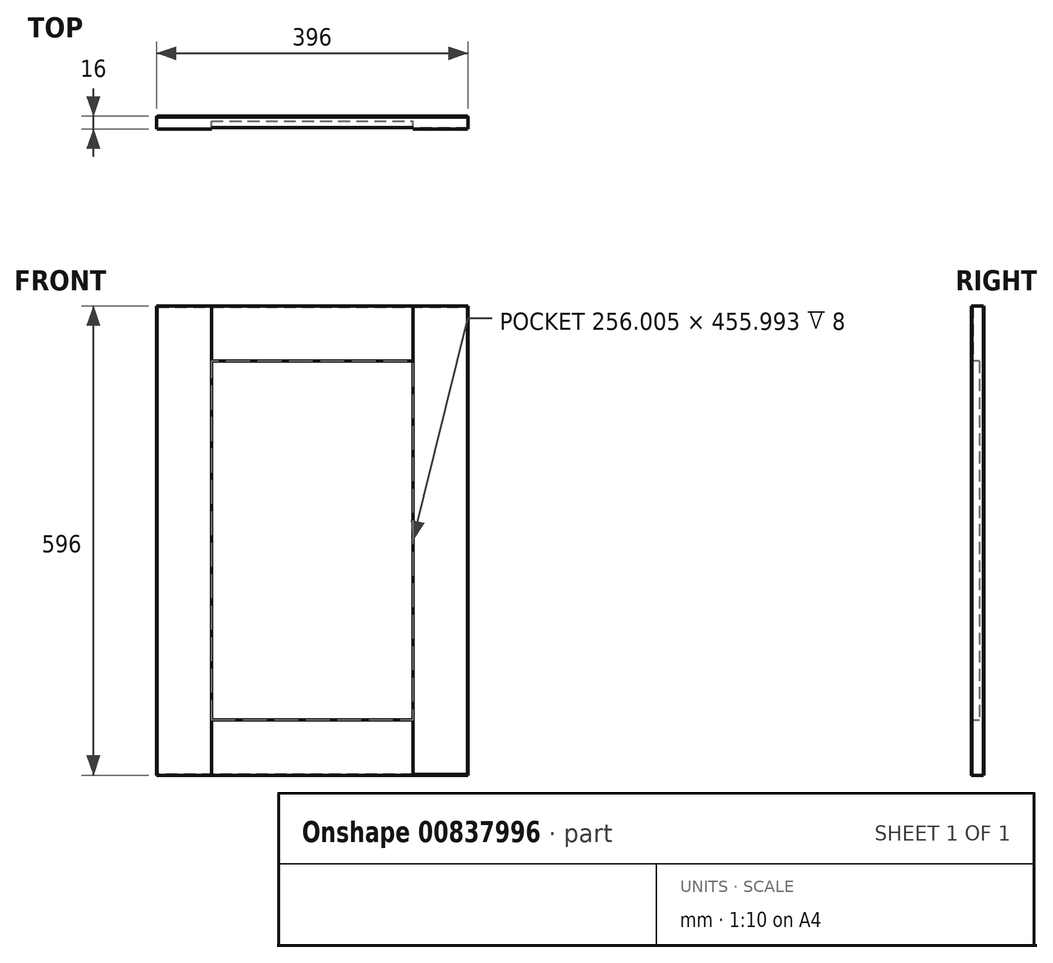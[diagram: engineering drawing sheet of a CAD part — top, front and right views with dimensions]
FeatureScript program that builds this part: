
annotation { "Feature Type Name" : "Feature", "Feature Type Description" : "" }
export const myFeature = defineFeature(function(context is Context, id is Id, definition is map)
    precondition{}
    {
        {
            var Q0;
            Q0=qCreatedBy(makeId("Front.planeOp"),FACE);
            var sketch = newSketch(context, id + "F0", { "sketchPlane" : qUnion([Q0])});
            skLineSegment(sketch, "E0.bottom", {"start": v(0, 0) * mm, "end": v(35.9, 0) * mm});
            skLineSegment(sketch, "E0.top", {"start": v(0, 30.12) * mm, "end": v(35.9, 30.12) * mm});
            skLineSegment(sketch, "E0.left", {"start": v(0, 0) * mm, "end": v(0, 30.12) * mm});
            skLineSegment(sketch, "E0.right", {"start": v(35.9, 0) * mm, "end": v(35.9, 30.12) * mm});
            skSolve(sketch);
        }
        {
            var Q0;
            Q0=makeQuery(id+"F0.imprint","IMPRINT",FACE,{"disambiguationData":[TD([[makeQuery(id+"F0.imprint","IMPRINT",EDGE,{"derivedFrom":sQuery(id+"F0.wireOp",EDGE,"E0.bottom")}),1.0]])]});
            extrude(context, id + "F1", {"entities" : qUnion([Q0]), "depth" : 16 * mm, "offsetDistance" : 25.4 * mm});
        }
        {
            var Q0;
            Q0=makeQuery(id+"F1.opExtrude","SWEPT_FACE",FACE,{"disambiguationData":[OSD([sQuery(id+"F0.wireOp",EDGE,"E0.left")])]});
            extrude(context, id + "F2", {"entities" : qUnion([Q0]), "operationType" : NewBodyOperationType.ADD, "oppositeDirection" : true, "depth" : 196 * mm, "offsetDistance" : 25 * mm});
        }
        {
            var Q0;
            {var subQ0=sQuery(id+"F0.wireOp",EDGE,"E0.bottom");Q0=makeQuery(id+"F2.boolean.opBoolean","MERGE",FACE,{"derivedFrom":[makeQuery(id+"F1.opExtrude","SWEPT_FACE",FACE,{"disambiguationData":[OSD([subQ0])]}),makeQuery(id+"F2.opExtrude","SWEPT_FACE",FACE,{"disambiguationData":[OSD([subQ0,sQuery(id+"F0.wireOp",EDGE,"E0.left")])]})]});}
            extrude(context, id + "F3", {"entities" : qUnion([Q0]), "operationType" : NewBodyOperationType.ADD, "oppositeDirection" : true, "depth" : 796 * mm, "offsetDistance" : 25 * mm});
        }
        {
            var Q0;
            {var subQ0=sQuery(id+"F0.wireOp",EDGE,"E0.left");var subQ1=sQuery(id+"F0.wireOp",EDGE,"E0.bottom");Q0=makeQuery(id+"F3.boolean.opBoolean","MERGE",FACE,{"derivedFrom":[makeQuery(id+"F2.boolean.opBoolean","MERGE",FACE,{"derivedFrom":[makeQuery(id+"F1.opExtrude","CAP_FACE",FACE,{"disambiguationData":[OSD([subQ1,sQuery(id+"F0.wireOp",EDGE,"E0.top"),subQ0,sQuery(id+"F0.wireOp",EDGE,"E0.right")])],"isStart":false}),makeQuery(id+"F2.opExtrude","SWEPT_FACE",FACE,{"disambiguationData":[OSD([subQ0]),TDD([makeQuery(id+"F1.opExtrude","CAP_EDGE",EDGE,{"disambiguationData":[OSD([subQ0])],"isStart":false})])]})]}),makeQuery(id+"F3.opExtrude","SWEPT_FACE",FACE,{"disambiguationData":[OSD([subQ1,subQ0]),TDD([makeQuery(id+"F2.boolean.opBoolean","MERGE",EDGE,{"derivedFrom":[makeQuery(id+"F1.opExtrude","CAP_EDGE",EDGE,{"disambiguationData":[OSD([subQ1])],"isStart":false}),makeQuery(id+"F2.opExtrude","SWEPT_EDGE",EDGE,{"disambiguationData":[OSD([subQ1,subQ0]),TDD([makeQuery(id+"F1.opExtrude","CAP_VERTEX",VERTEX,{"disambiguationData":[OSD([subQ1,subQ0])],"isStart":false})])]})]})])]})]});}
            var sketch = newSketch(context, id + "F4", { "sketchPlane" : qUnion([Q0])});
            skLineSegment(sketch, "E1.bottom", {"start": v(0, 796) * mm, "end": v(42.19, 796) * mm});
            skLineSegment(sketch, "E1.top", {"start": v(0, 751.57) * mm, "end": v(42.19, 751.57) * mm});
            skLineSegment(sketch, "E1.left", {"start": v(0, 796) * mm, "end": v(0, 751.57) * mm});
            skLineSegment(sketch, "E1.right", {"start": v(42.19, 796) * mm, "end": v(42.19, 751.57) * mm});
            skLineSegment(sketch, "E2.bottom", {"start": v(196, 796) * mm, "end": v(153.6, 796) * mm});
            skLineSegment(sketch, "E2.top", {"start": v(196, 746.75) * mm, "end": v(153.6, 746.75) * mm});
            skLineSegment(sketch, "E2.left", {"start": v(196, 796) * mm, "end": v(196, 746.75) * mm});
            skLineSegment(sketch, "E2.right", {"start": v(153.6, 796) * mm, "end": v(153.6, 746.75) * mm});
            skSolve(sketch);
        }
        {
            var Q0;
            Q0=makeQuery(id+"F4.imprint","IMPRINT",FACE,{"disambiguationData":[TD([[makeQuery(id+"F4.imprint","IMPRINT",EDGE,{"derivedFrom":sQuery(id+"F4.wireOp",EDGE,"E1.bottom")}),-1.0]])]});
            var Q1;
            Q1=makeQuery(id+"F4.imprint","IMPRINT",FACE,{"disambiguationData":[TD([[makeQuery(id+"F4.imprint","IMPRINT",EDGE,{"derivedFrom":sQuery(id+"F4.wireOp",EDGE,"E2.bottom")}),-1.0]])]});
            extrude(context, id + "F5", {"entities" : qUnion([Q0, Q1]), "operationType" : NewBodyOperationType.ADD, "depth" : 25 * mm, "offsetDistance" : 25 * mm});
        }
        {
            var Q0;
            {var subQ0=sQuery(id+"F0.wireOp",EDGE,"E0.left");var subQ1=sQuery(id+"F0.wireOp",EDGE,"E0.bottom");Q0=makeQuery(id+"F3.boolean.opBoolean","MERGE",FACE,{"derivedFrom":[makeQuery(id+"F2.boolean.opBoolean","MERGE",FACE,{"derivedFrom":[makeQuery(id+"F1.opExtrude","CAP_FACE",FACE,{"disambiguationData":[OSD([subQ1,sQuery(id+"F0.wireOp",EDGE,"E0.top"),subQ0,sQuery(id+"F0.wireOp",EDGE,"E0.right")])],"isStart":false}),makeQuery(id+"F2.opExtrude","SWEPT_FACE",FACE,{"disambiguationData":[OSD([subQ0]),TDD([makeQuery(id+"F1.opExtrude","CAP_EDGE",EDGE,{"disambiguationData":[OSD([subQ0])],"isStart":false})])]})]}),makeQuery(id+"F3.opExtrude","SWEPT_FACE",FACE,{"disambiguationData":[OSD([subQ1,subQ0]),TDD([makeQuery(id+"F2.boolean.opBoolean","MERGE",EDGE,{"derivedFrom":[makeQuery(id+"F1.opExtrude","CAP_EDGE",EDGE,{"disambiguationData":[OSD([subQ1])],"isStart":false}),makeQuery(id+"F2.opExtrude","SWEPT_EDGE",EDGE,{"disambiguationData":[OSD([subQ1,subQ0]),TDD([makeQuery(id+"F1.opExtrude","CAP_VERTEX",VERTEX,{"disambiguationData":[OSD([subQ1,subQ0])],"isStart":false})])]})]})])]})]});}
            var sketch = newSketch(context, id + "F6", { "sketchPlane" : qUnion([Q0])});
            skLineSegment(sketch, "E3.bottom", {"start": v(196, 0) * mm, "end": v(163.38, 0) * mm});
            skLineSegment(sketch, "E3.top", {"start": v(196, 46.55) * mm, "end": v(163.38, 46.55) * mm});
            skLineSegment(sketch, "E3.left", {"start": v(196, 0) * mm, "end": v(196, 46.55) * mm});
            skLineSegment(sketch, "E3.right", {"start": v(163.38, 0) * mm, "end": v(163.38, 46.55) * mm});
            skLineSegment(sketch, "E4.bottom", {"start": v(0, 0) * mm, "end": v(50.28, 0) * mm});
            skLineSegment(sketch, "E4.top", {"start": v(0, 44.4) * mm, "end": v(50.28, 44.4) * mm});
            skLineSegment(sketch, "E4.left", {"start": v(0, 0) * mm, "end": v(0, 44.4) * mm});
            skLineSegment(sketch, "E4.right", {"start": v(50.28, 0) * mm, "end": v(50.28, 44.4) * mm});
            skSolve(sketch);
        }
        {
            var Q0;
            Q0=makeQuery(id+"F6.imprint","IMPRINT",FACE,{"disambiguationData":[TD([[makeQuery(id+"F6.imprint","IMPRINT",EDGE,{"derivedFrom":sQuery(id+"F6.wireOp",EDGE,"E3.bottom")}),1.0]])]});
            var Q1;
            Q1=makeQuery(id+"F6.imprint","IMPRINT",FACE,{"disambiguationData":[TD([[makeQuery(id+"F6.imprint","IMPRINT",EDGE,{"derivedFrom":sQuery(id+"F6.wireOp",EDGE,"E4.bottom")}),1.0]])]});
            extrude(context, id + "F7", {"entities" : qUnion([Q0, Q1]), "operationType" : NewBodyOperationType.ADD, "depth" : 25 * mm, "offsetDistance" : 25 * mm});
        }
        {
            var Q0;
            Q0=makeQuery(id+"F7.opExtrude","SWEPT_FACE",FACE,{"disambiguationData":[OSD([sQuery(id+"F6.wireOp",EDGE,"E4.right")])]});
            extrude(context, id + "F8", {"entities" : qUnion([Q0]), "operationType" : NewBodyOperationType.ADD, "depth" : 19.72 * mm, "offsetDistance" : 25 * mm});
        }
        {
            var Q0;
            {var subQ0=sQuery(id+"F6.wireOp",EDGE,"E4.top");Q0=makeQuery(id+"F8.boolean.opBoolean","MERGE",FACE,{"derivedFrom":[makeQuery(id+"F7.opExtrude","SWEPT_FACE",FACE,{"disambiguationData":[OSD([subQ0])]}),makeQuery(id+"F8.opExtrude","SWEPT_FACE",FACE,{"disambiguationData":[OSD([subQ0,sQuery(id+"F6.wireOp",EDGE,"E4.right")])]})]});}
            extrude(context, id + "F9", {"entities" : qUnion([Q0]), "operationType" : NewBodyOperationType.ADD, "depth" : 25.6 * mm, "offsetDistance" : 25 * mm});
        }
        {
            var Q0;
            Q0=makeQuery(id+"F7.opExtrude","SWEPT_FACE",FACE,{"disambiguationData":[OSD([sQuery(id+"F6.wireOp",EDGE,"E3.right")])]});
            extrude(context, id + "F10", {"entities" : qUnion([Q0]), "operationType" : NewBodyOperationType.ADD, "depth" : 37.38 * mm, "offsetDistance" : 25 * mm});
        }
        {
            var Q0;
            {var subQ0=sQuery(id+"F6.wireOp",EDGE,"E3.top");Q0=makeQuery(id+"F10.boolean.opBoolean","MERGE",FACE,{"derivedFrom":[makeQuery(id+"F7.opExtrude","SWEPT_FACE",FACE,{"disambiguationData":[OSD([subQ0])]}),makeQuery(id+"F10.opExtrude","SWEPT_FACE",FACE,{"disambiguationData":[OSD([subQ0,sQuery(id+"F6.wireOp",EDGE,"E3.right")])]})]});}
            extrude(context, id + "F11", {"entities" : qUnion([Q0]), "operationType" : NewBodyOperationType.ADD, "depth" : 23.45 * mm, "offsetDistance" : 25 * mm});
        }
        {
            var Q0;
            Q0=makeQuery(id+"F5.opExtrude","SWEPT_FACE",FACE,{"disambiguationData":[OSD([sQuery(id+"F4.wireOp",EDGE,"E1.right")])]});
            extrude(context, id + "F12", {"entities" : qUnion([Q0]), "operationType" : NewBodyOperationType.ADD, "depth" : 27.8 * mm, "offsetDistance" : 25 * mm});
        }
        {
            var Q0;
            {var subQ0=sQuery(id+"F4.wireOp",EDGE,"E1.top");Q0=makeQuery(id+"F12.boolean.opBoolean","MERGE",FACE,{"derivedFrom":[makeQuery(id+"F5.opExtrude","SWEPT_FACE",FACE,{"disambiguationData":[OSD([subQ0])]}),makeQuery(id+"F12.opExtrude","SWEPT_FACE",FACE,{"disambiguationData":[OSD([subQ0,sQuery(id+"F4.wireOp",EDGE,"E1.right")])]})]});}
            extrude(context, id + "F13", {"entities" : qUnion([Q0]), "operationType" : NewBodyOperationType.ADD, "depth" : 25.57 * mm, "offsetDistance" : 25 * mm});
        }
        {
            var Q0;
            Q0=makeQuery(id+"F5.opExtrude","SWEPT_FACE",FACE,{"disambiguationData":[OSD([sQuery(id+"F4.wireOp",EDGE,"E2.top")])]});
            extrude(context, id + "F14", {"entities" : qUnion([Q0]), "operationType" : NewBodyOperationType.ADD, "depth" : 20.75 * mm, "offsetDistance" : 25 * mm});
        }
        {
            var Q0;
            {var subQ0=sQuery(id+"F4.wireOp",EDGE,"E2.right");Q0=makeQuery(id+"F14.boolean.opBoolean","MERGE",FACE,{"derivedFrom":[makeQuery(id+"F5.opExtrude","SWEPT_FACE",FACE,{"disambiguationData":[OSD([subQ0])]}),makeQuery(id+"F14.opExtrude","SWEPT_FACE",FACE,{"disambiguationData":[OSD([sQuery(id+"F4.wireOp",EDGE,"E2.top"),subQ0])]})]});}
            extrude(context, id + "F15", {"entities" : qUnion([Q0]), "operationType" : NewBodyOperationType.ADD, "depth" : 27.6 * mm, "offsetDistance" : 25 * mm});
        }
        {
            var Q0;
            {var subQ0=sQuery(id+"F0.wireOp",EDGE,"E0.left");var subQ1=sQuery(id+"F0.wireOp",EDGE,"E0.bottom");Q0=makeQuery(id+"F3.boolean.opBoolean","MERGE",FACE,{"derivedFrom":[makeQuery(id+"F2.boolean.opBoolean","MERGE",FACE,{"derivedFrom":[makeQuery(id+"F1.opExtrude","CAP_FACE",FACE,{"disambiguationData":[OSD([subQ1,sQuery(id+"F0.wireOp",EDGE,"E0.top"),subQ0,sQuery(id+"F0.wireOp",EDGE,"E0.right")])],"isStart":false}),makeQuery(id+"F2.opExtrude","SWEPT_FACE",FACE,{"disambiguationData":[OSD([subQ0]),TDD([makeQuery(id+"F1.opExtrude","CAP_EDGE",EDGE,{"disambiguationData":[OSD([subQ0])],"isStart":false})])]})]}),makeQuery(id+"F3.opExtrude","SWEPT_FACE",FACE,{"disambiguationData":[OSD([subQ1,subQ0]),TDD([makeQuery(id+"F2.boolean.opBoolean","MERGE",EDGE,{"derivedFrom":[makeQuery(id+"F1.opExtrude","CAP_EDGE",EDGE,{"disambiguationData":[OSD([subQ1])],"isStart":false}),makeQuery(id+"F2.opExtrude","SWEPT_EDGE",EDGE,{"disambiguationData":[OSD([subQ1,subQ0]),TDD([makeQuery(id+"F1.opExtrude","CAP_VERTEX",VERTEX,{"disambiguationData":[OSD([subQ1,subQ0])],"isStart":false})])]})]})])]})]});}
            var sketch = newSketch(context, id + "F16", { "sketchPlane" : qUnion([Q0])});
            skLineSegment(sketch, "E5.bottom", {"start": v(70, 726) * mm, "end": v(126, 726) * mm});
            skLineSegment(sketch, "E5.top", {"start": v(70, 70) * mm, "end": v(126, 70) * mm});
            skLineSegment(sketch, "E5.left", {"start": v(70, 726) * mm, "end": v(70, 70) * mm});
            skLineSegment(sketch, "E5.right", {"start": v(126, 726) * mm, "end": v(126, 70) * mm});
            skSolve(sketch);
        }
        {
            var Q0;
            Q0=makeQuery(id+"F16.imprint","IMPRINT",FACE,{"disambiguationData":[TD([[makeQuery(id+"F16.imprint","IMPRINT",EDGE,{"derivedFrom":sQuery(id+"F16.wireOp",EDGE,"E5.top")}),1.0]])]});
            extrude(context, id + "F17", {"entities" : qUnion([Q0]), "operationType" : NewBodyOperationType.REMOVE, "oppositeDirection" : true, "depth" : 10 * mm, "offsetDistance" : 25 * mm});
        }
        {
            var Q0;
            {var subQ2=sQuery(id+"F0.wireOp",EDGE,"E0.left");var subQ3=sQuery(id+"F0.wireOp",EDGE,"E0.bottom");var subQ4=makeQuery(id+"F1.opExtrude","CAP_FACE",FACE,{"disambiguationData":[OSD([subQ3,sQuery(id+"F0.wireOp",EDGE,"E0.top"),subQ2,sQuery(id+"F0.wireOp",EDGE,"E0.right")])],"isStart":false});var subQ7=makeQuery(id+"F3.opExtrude","SWEPT_FACE",FACE,{"disambiguationData":[OSD([subQ3,subQ2]),TDD([makeQuery(id+"F2.boolean.opBoolean","MERGE",EDGE,{"derivedFrom":[makeQuery(id+"F1.opExtrude","CAP_EDGE",EDGE,{"disambiguationData":[OSD([subQ3])],"isStart":false}),makeQuery(id+"F2.opExtrude","SWEPT_EDGE",EDGE,{"disambiguationData":[OSD([subQ3,subQ2]),TDD([makeQuery(id+"F1.opExtrude","CAP_VERTEX",VERTEX,{"disambiguationData":[OSD([subQ3,subQ2])],"isStart":false})])]})]})])]});var subQ8=makeQuery(id+"F2.opExtrude","SWEPT_FACE",FACE,{"disambiguationData":[OSD([subQ2]),TDD([makeQuery(id+"F1.opExtrude","CAP_EDGE",EDGE,{"disambiguationData":[OSD([subQ2])],"isStart":false})])]});Q0=makeQuery(id+"F17.boolean.opBoolean","SPLIT",FACE,{"disambiguationData":[TD([makeQuery(id+"F1.opExtrude","SWEPT_FACE",FACE,{"disambiguationData":[OSD([subQ3])]})])],"derivedFrom":makeQuery(id+"F3.boolean.opBoolean","MERGE",FACE,{"derivedFrom":[makeQuery(id+"F2.boolean.opBoolean","MERGE",FACE,{"derivedFrom":[subQ4,subQ8]}),subQ7]})});}
            var Q1;
            {var subQ2=sQuery(id+"F4.wireOp",EDGE,"E1.bottom");var subQ3=sQuery(id+"F0.wireOp",EDGE,"E0.left");var subQ4=sQuery(id+"F0.wireOp",EDGE,"E0.bottom");var subQ6=makeQuery(id+"F1.opExtrude","CAP_FACE",FACE,{"disambiguationData":[OSD([subQ4,sQuery(id+"F0.wireOp",EDGE,"E0.top"),subQ3,sQuery(id+"F0.wireOp",EDGE,"E0.right")])],"isStart":false});var subQ7=makeQuery(id+"F2.opExtrude","SWEPT_FACE",FACE,{"disambiguationData":[OSD([subQ3]),TDD([makeQuery(id+"F1.opExtrude","CAP_EDGE",EDGE,{"disambiguationData":[OSD([subQ3])],"isStart":false})])]});var subQ8=makeQuery(id+"F3.opExtrude","SWEPT_FACE",FACE,{"disambiguationData":[OSD([subQ4,subQ3]),TDD([makeQuery(id+"F2.boolean.opBoolean","MERGE",EDGE,{"derivedFrom":[makeQuery(id+"F1.opExtrude","CAP_EDGE",EDGE,{"disambiguationData":[OSD([subQ4])],"isStart":false}),makeQuery(id+"F2.opExtrude","SWEPT_EDGE",EDGE,{"disambiguationData":[OSD([subQ4,subQ3]),TDD([makeQuery(id+"F1.opExtrude","CAP_VERTEX",VERTEX,{"disambiguationData":[OSD([subQ4,subQ3])],"isStart":false})])]})]})])]});Q1=makeQuery(id+"F17.boolean.opBoolean","SPLIT",FACE,{"disambiguationData":[TD([makeQuery(id+"F5.opExtrude","SWEPT_FACE",FACE,{"disambiguationData":[OSD([subQ2])]})])],"derivedFrom":makeQuery(id+"F3.boolean.opBoolean","MERGE",FACE,{"derivedFrom":[makeQuery(id+"F2.boolean.opBoolean","MERGE",FACE,{"derivedFrom":[subQ6,subQ7]}),subQ8]})});}
            extrude(context, id + "F18", {"entities" : qUnion([Q0, Q1]), "operationType" : NewBodyOperationType.REMOVE, "oppositeDirection" : true, "depth" : 2 * mm, "offsetDistance" : 25 * mm});
        }
        {
            var Q0;
            {var subQ0=sQuery(id+"F4.wireOp",EDGE,"E1.right");var subQ1=sQuery(id+"F4.wireOp",EDGE,"E1.top");Q0=makeQuery(id+"F13.boolean.opBoolean","MERGE",FACE,{"derivedFrom":[makeQuery(id+"F12.boolean.opBoolean","MERGE",FACE,{"derivedFrom":[makeQuery(id+"F5.opExtrude","CAP_FACE",FACE,{"disambiguationData":[OSD([sQuery(id+"F4.wireOp",EDGE,"E1.bottom"),subQ1,sQuery(id+"F4.wireOp",EDGE,"E1.left"),subQ0])],"isStart":false}),makeQuery(id+"F12.opExtrude","SWEPT_FACE",FACE,{"disambiguationData":[OSD([subQ0]),TDD([makeQuery(id+"F5.opExtrude","CAP_EDGE",EDGE,{"disambiguationData":[OSD([subQ0])],"isStart":false})])]})]}),makeQuery(id+"F13.opExtrude","SWEPT_FACE",FACE,{"disambiguationData":[OSD([subQ1,subQ0]),TDD([makeQuery(id+"F12.boolean.opBoolean","MERGE",EDGE,{"derivedFrom":[makeQuery(id+"F5.opExtrude","CAP_EDGE",EDGE,{"disambiguationData":[OSD([subQ1])],"isStart":false}),makeQuery(id+"F12.opExtrude","SWEPT_EDGE",EDGE,{"disambiguationData":[OSD([subQ1,subQ0]),TDD([makeQuery(id+"F5.opExtrude","CAP_VERTEX",VERTEX,{"disambiguationData":[OSD([subQ1,subQ0])],"isStart":false})])]})]})])]})]});}
            var Q1;
            {var subQ0=sQuery(id+"F4.wireOp",EDGE,"E2.right");var subQ1=sQuery(id+"F4.wireOp",EDGE,"E2.top");Q1=makeQuery(id+"F15.boolean.opBoolean","MERGE",FACE,{"derivedFrom":[makeQuery(id+"F14.boolean.opBoolean","MERGE",FACE,{"derivedFrom":[makeQuery(id+"F5.opExtrude","CAP_FACE",FACE,{"disambiguationData":[OSD([sQuery(id+"F4.wireOp",EDGE,"E2.bottom"),subQ1,sQuery(id+"F4.wireOp",EDGE,"E2.left"),subQ0])],"isStart":false}),makeQuery(id+"F14.opExtrude","SWEPT_FACE",FACE,{"disambiguationData":[OSD([subQ1]),TDD([makeQuery(id+"F5.opExtrude","CAP_EDGE",EDGE,{"disambiguationData":[OSD([subQ1])],"isStart":false})])]})]}),makeQuery(id+"F15.opExtrude","SWEPT_FACE",FACE,{"disambiguationData":[OSD([subQ1,subQ0]),TDD([makeQuery(id+"F14.boolean.opBoolean","MERGE",EDGE,{"derivedFrom":[makeQuery(id+"F5.opExtrude","CAP_EDGE",EDGE,{"disambiguationData":[OSD([subQ0])],"isStart":false}),makeQuery(id+"F14.opExtrude","SWEPT_EDGE",EDGE,{"disambiguationData":[OSD([subQ1,subQ0]),TDD([makeQuery(id+"F5.opExtrude","CAP_VERTEX",VERTEX,{"disambiguationData":[OSD([subQ1,subQ0])],"isStart":false})])]})]})])]})]});}
            var Q2;
            {var subQ0=sQuery(id+"F6.wireOp",EDGE,"E4.right");var subQ1=sQuery(id+"F6.wireOp",EDGE,"E4.top");Q2=makeQuery(id+"F9.boolean.opBoolean","MERGE",FACE,{"derivedFrom":[makeQuery(id+"F8.boolean.opBoolean","MERGE",FACE,{"derivedFrom":[makeQuery(id+"F7.opExtrude","CAP_FACE",FACE,{"disambiguationData":[OSD([sQuery(id+"F6.wireOp",EDGE,"E4.bottom"),subQ1,sQuery(id+"F6.wireOp",EDGE,"E4.left"),subQ0])],"isStart":false}),makeQuery(id+"F8.opExtrude","SWEPT_FACE",FACE,{"disambiguationData":[OSD([subQ0]),TDD([makeQuery(id+"F7.opExtrude","CAP_EDGE",EDGE,{"disambiguationData":[OSD([subQ0])],"isStart":false})])]})]}),makeQuery(id+"F9.opExtrude","SWEPT_FACE",FACE,{"disambiguationData":[OSD([subQ1,subQ0]),TDD([makeQuery(id+"F8.boolean.opBoolean","MERGE",EDGE,{"derivedFrom":[makeQuery(id+"F7.opExtrude","CAP_EDGE",EDGE,{"disambiguationData":[OSD([subQ1])],"isStart":false}),makeQuery(id+"F8.opExtrude","SWEPT_EDGE",EDGE,{"disambiguationData":[OSD([subQ1,subQ0]),TDD([makeQuery(id+"F7.opExtrude","CAP_VERTEX",VERTEX,{"disambiguationData":[OSD([subQ1,subQ0])],"isStart":false})])]})]})])]})]});}
            var Q3;
            {var subQ0=sQuery(id+"F6.wireOp",EDGE,"E3.right");var subQ1=sQuery(id+"F6.wireOp",EDGE,"E3.top");Q3=makeQuery(id+"F11.boolean.opBoolean","MERGE",FACE,{"derivedFrom":[makeQuery(id+"F10.boolean.opBoolean","MERGE",FACE,{"derivedFrom":[makeQuery(id+"F7.opExtrude","CAP_FACE",FACE,{"disambiguationData":[OSD([sQuery(id+"F6.wireOp",EDGE,"E3.bottom"),subQ1,sQuery(id+"F6.wireOp",EDGE,"E3.left"),subQ0])],"isStart":false}),makeQuery(id+"F10.opExtrude","SWEPT_FACE",FACE,{"disambiguationData":[OSD([subQ0]),TDD([makeQuery(id+"F7.opExtrude","CAP_EDGE",EDGE,{"disambiguationData":[OSD([subQ0])],"isStart":false})])]})]}),makeQuery(id+"F11.opExtrude","SWEPT_FACE",FACE,{"disambiguationData":[OSD([subQ1,subQ0]),TDD([makeQuery(id+"F10.boolean.opBoolean","MERGE",EDGE,{"derivedFrom":[makeQuery(id+"F7.opExtrude","CAP_EDGE",EDGE,{"disambiguationData":[OSD([subQ1])],"isStart":false}),makeQuery(id+"F10.opExtrude","SWEPT_EDGE",EDGE,{"disambiguationData":[OSD([subQ1,subQ0]),TDD([makeQuery(id+"F7.opExtrude","CAP_VERTEX",VERTEX,{"disambiguationData":[OSD([subQ1,subQ0])],"isStart":false})])]})]})])]})]});}
            extrude(context, id + "F19", {"entities" : qUnion([Q0, Q1, Q2, Q3]), "operationType" : NewBodyOperationType.REMOVE, "oppositeDirection" : true, "depth" : 25 * mm, "offsetDistance" : 25 * mm});
        }
        {
            var Q0;
            {var subQ0=sQuery(id+"F4.wireOp",EDGE,"E2.left");var subQ1=sQuery(id+"F0.wireOp",EDGE,"E0.left");var subQ2=sQuery(id+"F0.wireOp",EDGE,"E0.bottom");var subQ3=sQuery(id+"F6.wireOp",EDGE,"E3.left");Q0=makeQuery(id+"F14.boolean.opBoolean","MERGE",FACE,{"derivedFrom":[makeQuery(id+"F11.boolean.opBoolean","MERGE",FACE,{"derivedFrom":[makeQuery(id+"F7.boolean.opBoolean","MERGE",FACE,{"derivedFrom":[makeQuery(id+"F5.boolean.opBoolean","MERGE",FACE,{"derivedFrom":[makeQuery(id+"F3.boolean.opBoolean","MERGE",FACE,{"derivedFrom":[makeQuery(id+"F2.opExtrude","CAP_FACE",FACE,{"disambiguationData":[OSD([subQ1])],"isStart":false}),makeQuery(id+"F3.opExtrude","SWEPT_FACE",FACE,{"disambiguationData":[OSD([subQ2,subQ1]),TDD([makeQuery(id+"F2.opExtrude","CAP_EDGE",EDGE,{"disambiguationData":[OSD([subQ2,subQ1])],"isStart":false})])]})]}),makeQuery(id+"F5.opExtrude","SWEPT_FACE",FACE,{"disambiguationData":[OSD([subQ0])]})]}),makeQuery(id+"F7.opExtrude","SWEPT_FACE",FACE,{"disambiguationData":[OSD([subQ3])]})]}),makeQuery(id+"F11.opExtrude","SWEPT_FACE",FACE,{"disambiguationData":[OSD([subQ2,subQ1,sQuery(id+"F6.wireOp",EDGE,"E3.top"),subQ3])]})]}),makeQuery(id+"F14.opExtrude","SWEPT_FACE",FACE,{"disambiguationData":[OSD([subQ2,subQ1,sQuery(id+"F4.wireOp",EDGE,"E2.top"),subQ0])]})]});}
            extrude(context, id + "F20", {"entities" : qUnion([Q0]), "operationType" : NewBodyOperationType.ADD, "depth" : 200 * mm, "offsetDistance" : 25 * mm});
        }
        {
            var Q0;
            {var subQ0=sQuery(id+"F4.wireOp",EDGE,"E2.right");var subQ1=sQuery(id+"F4.wireOp",EDGE,"E2.top");Q0=makeQuery(id+"F18.boolean.opBoolean","MERGE",FACE,{"derivedFrom":[makeQuery(id+"F15.opExtrude","CAP_FACE",FACE,{"disambiguationData":[OSD([subQ1,subQ0])],"isStart":false}),makeQuery(id+"F18.opExtrude","SWEPT_FACE",FACE,{"disambiguationData":[OSD([subQ1,subQ0])]})]});}
            var Q1;
            {var subQ0=sQuery(id+"F6.wireOp",EDGE,"E3.right");var subQ1=sQuery(id+"F6.wireOp",EDGE,"E3.top");Q1=makeQuery(id+"F18.boolean.opBoolean","MERGE",FACE,{"derivedFrom":[makeQuery(id+"F11.boolean.opBoolean","MERGE",FACE,{"derivedFrom":[makeQuery(id+"F10.opExtrude","CAP_FACE",FACE,{"disambiguationData":[OSD([subQ0])],"isStart":false}),makeQuery(id+"F11.opExtrude","SWEPT_FACE",FACE,{"disambiguationData":[OSD([subQ1,subQ0]),TDD([makeQuery(id+"F10.opExtrude","CAP_EDGE",EDGE,{"disambiguationData":[OSD([subQ1,subQ0])],"isStart":false})])]})]}),makeQuery(id+"F17.boolean.opBoolean","COPY",FACE,{"derivedFrom":makeQuery(id+"F17.opExtrude","SWEPT_FACE",FACE,{"disambiguationData":[OSD([sQuery(id+"F16.wireOp",EDGE,"E5.right")])]})}),makeQuery(id+"F18.opExtrude","SWEPT_FACE",FACE,{"disambiguationData":[OSD([subQ1,subQ0])]})]});}
            extrude(context, id + "F21", {"entities" : qUnion([Q0, Q1]), "operationType" : NewBodyOperationType.REMOVE, "oppositeDirection" : true, "depth" : 200 * mm, "offsetDistance" : 25 * mm});
        }
        {
            var Q0;
            {var subQ0=sQuery(id+"F4.wireOp",EDGE,"E2.bottom");var subQ1=sQuery(id+"F0.wireOp",EDGE,"E0.left");var subQ2=sQuery(id+"F0.wireOp",EDGE,"E0.bottom");var subQ3=sQuery(id+"F4.wireOp",EDGE,"E1.bottom");Q0=makeQuery(id+"F20.boolean.opBoolean","MERGE",FACE,{"derivedFrom":[makeQuery(id+"F15.boolean.opBoolean","MERGE",FACE,{"derivedFrom":[makeQuery(id+"F12.boolean.opBoolean","MERGE",FACE,{"derivedFrom":[makeQuery(id+"F5.boolean.opBoolean","MERGE",FACE,{"derivedFrom":[makeQuery(id+"F3.opExtrude","CAP_FACE",FACE,{"disambiguationData":[OSD([subQ2,subQ1])],"isStart":false}),makeQuery(id+"F5.opExtrude","SWEPT_FACE",FACE,{"disambiguationData":[OSD([subQ3])]}),makeQuery(id+"F5.opExtrude","SWEPT_FACE",FACE,{"disambiguationData":[OSD([subQ0])]})]}),makeQuery(id+"F12.opExtrude","SWEPT_FACE",FACE,{"disambiguationData":[OSD([subQ2,subQ1,subQ3,sQuery(id+"F4.wireOp",EDGE,"E1.right")])]})]}),makeQuery(id+"F15.opExtrude","SWEPT_FACE",FACE,{"disambiguationData":[OSD([subQ2,subQ1,subQ0,sQuery(id+"F4.wireOp",EDGE,"E2.right")])]})]}),makeQuery(id+"F20.opExtrude","SWEPT_FACE",FACE,{"disambiguationData":[OSD([subQ2,subQ1,subQ0,sQuery(id+"F4.wireOp",EDGE,"E2.left")])]})]});}
            extrude(context, id + "F22", {"entities" : qUnion([Q0]), "operationType" : NewBodyOperationType.ADD, "depth" : 200 * mm, "offsetDistance" : 25 * mm});
        }
        {
            var Q0;
            Q0=makeQuery(id+"F17.boolean.opBoolean","COPY",FACE,{"derivedFrom":makeQuery(id+"F17.opExtrude","SWEPT_FACE",FACE,{"disambiguationData":[OSD([sQuery(id+"F16.wireOp",EDGE,"E5.bottom")])]})});
            var Q1;
            {var subQ0=sQuery(id+"F16.wireOp",EDGE,"E5.right");var subQ1=sQuery(id+"F16.wireOp",EDGE,"E5.bottom");var subQ2=sQuery(id+"F4.wireOp",EDGE,"E2.right");var subQ3=sQuery(id+"F4.wireOp",EDGE,"E2.top");var subQ4=makeQuery(id+"F17.boolean.opBoolean","COPY",EDGE,{"derivedFrom":makeQuery(id+"F17.opExtrude","SWEPT_EDGE",EDGE,{"disambiguationData":[OSD([subQ3,subQ2,subQ1,subQ0])]})});Q1=makeQuery(id+"F21.boolean.opBoolean","COPY",FACE,{"derivedFrom":makeQuery(id+"F21.opExtrude","SWEPT_FACE",FACE,{"disambiguationData":[OSD([subQ3,subQ2,subQ1,subQ0]),TDD([makeQuery(id+"F18.boolean.opBoolean","MERGE",EDGE,{"derivedFrom":[subQ4,makeQuery(id+"F18.opExtrude","SWEPT_EDGE",EDGE,{"disambiguationData":[OSD([subQ3,subQ2,subQ1,subQ0])]})]}),makeQuery(id+"F18.boolean.opBoolean","SPLIT",EDGE,{"derivedFrom":subQ4})])]})});}
            extrude(context, id + "F23", {"entities" : qUnion([Q0, Q1]), "operationType" : NewBodyOperationType.REMOVE, "oppositeDirection" : true, "depth" : 200 * mm, "offsetDistance" : 25 * mm});
        }
        {
            var Q0;
            Q0=makeQuery(id+"F23.boolean.opBoolean","COPY",FACE,{"derivedFrom":makeQuery(id+"F23.opExtrude","CAP_FACE",FACE,{"disambiguationData":[OSD([sQuery(id+"F16.wireOp",EDGE,"E5.bottom")])],"isStart":false})});
            var Q1;
            Q1=makeQuery(id+"F23.boolean.opBoolean","COPY",FACE,{"derivedFrom":makeQuery(id+"F23.opExtrude","CAP_FACE",FACE,{"disambiguationData":[OSD([sQuery(id+"F4.wireOp",EDGE,"E2.top"),sQuery(id+"F4.wireOp",EDGE,"E2.right"),sQuery(id+"F16.wireOp",EDGE,"E5.bottom"),sQuery(id+"F16.wireOp",EDGE,"E5.right")])],"isStart":false})});
            extrude(context, id + "F24", {"entities" : qUnion([Q0, Q1]), "operationType" : NewBodyOperationType.ADD, "depth" : 400 * mm, "offsetDistance" : 25 * mm});
        }
        {
            var Q0;
            Q0=makeQuery(id+"F22.opExtrude","CAP_FACE",FACE,{"disambiguationData":[OSD([sQuery(id+"F0.wireOp",EDGE,"E0.bottom"),sQuery(id+"F0.wireOp",EDGE,"E0.left"),sQuery(id+"F4.wireOp",EDGE,"E1.bottom"),sQuery(id+"F4.wireOp",EDGE,"E1.right"),sQuery(id+"F4.wireOp",EDGE,"E2.bottom"),sQuery(id+"F4.wireOp",EDGE,"E2.left"),sQuery(id+"F4.wireOp",EDGE,"E2.right")])],"isStart":false});
            extrude(context, id + "F25", {"entities" : qUnion([Q0]), "operationType" : NewBodyOperationType.REMOVE, "oppositeDirection" : true, "depth" : 400 * mm, "offsetDistance" : 25 * mm});
        }
        {
            var Q0;
            {var subQ0=sQuery(id+"F4.wireOp",EDGE,"E1.right");var subQ1=sQuery(id+"F4.wireOp",EDGE,"E1.bottom");var subQ2=sQuery(id+"F0.wireOp",EDGE,"E0.left");var subQ3=sQuery(id+"F0.wireOp",EDGE,"E0.bottom");Q0=makeQuery(id+"F25.boolean.opBoolean","COPY",EDGE,{"derivedFrom":makeQuery(id+"F25.opExtrude","CAP_EDGE",EDGE,{"disambiguationData":[OSD([subQ3,subQ2,subQ1,subQ0]),TDD([makeQuery(id+"F22.opExtrude","CAP_EDGE",EDGE,{"disambiguationData":[OSD([subQ3,subQ2,subQ1,subQ0]),TDD([makeQuery(id+"F19.boolean.opBoolean","COPY",EDGE,{"derivedFrom":makeQuery(id+"F19.opExtrude","CAP_EDGE",EDGE,{"disambiguationData":[OSD([subQ3,subQ2,subQ1,subQ0])],"isStart":false})})])],"isStart":false})])],"isStart":false})});}
            var Q1;
            {var subQ0=sQuery(id+"F4.wireOp",EDGE,"E1.left");var subQ1=sQuery(id+"F0.wireOp",EDGE,"E0.left");var subQ2=sQuery(id+"F0.wireOp",EDGE,"E0.bottom");Q1=makeQuery(id+"F22.boolean.opBoolean","MERGE",EDGE,{"derivedFrom":[makeQuery(id+"F19.boolean.opBoolean","MERGE",EDGE,{"derivedFrom":[makeQuery(id+"F3.boolean.opBoolean","MERGE",EDGE,{"derivedFrom":[makeQuery(id+"F1.opExtrude","CAP_EDGE",EDGE,{"disambiguationData":[OSD([subQ1])],"isStart":false}),makeQuery(id+"F3.opExtrude","SWEPT_EDGE",EDGE,{"disambiguationData":[OSD([subQ2,subQ1]),TDD([makeQuery(id+"F1.opExtrude","CAP_VERTEX",VERTEX,{"disambiguationData":[OSD([subQ2,subQ1])],"isStart":false})])]})]}),makeQuery(id+"F19.opExtrude","CAP_EDGE",EDGE,{"disambiguationData":[OSD([subQ2,subQ1,sQuery(id+"F6.wireOp",EDGE,"E4.top"),sQuery(id+"F6.wireOp",EDGE,"E4.left")])],"isStart":false}),makeQuery(id+"F19.opExtrude","CAP_EDGE",EDGE,{"disambiguationData":[OSD([subQ2,subQ1,sQuery(id+"F4.wireOp",EDGE,"E1.top"),subQ0])],"isStart":false})]}),makeQuery(id+"F22.opExtrude","SWEPT_EDGE",EDGE,{"disambiguationData":[OSD([sQuery(id+"F4.wireOp",EDGE,"E1.bottom"),subQ0])]})]});}
            var Q2;
            {var subQ0=sQuery(id+"F4.wireOp",EDGE,"E2.left");Q2=makeQuery(id+"F22.boolean.opBoolean","MERGE",EDGE,{"derivedFrom":[makeQuery(id+"F20.opExtrude","CAP_EDGE",EDGE,{"disambiguationData":[OSD([sQuery(id+"F0.wireOp",EDGE,"E0.bottom"),sQuery(id+"F0.wireOp",EDGE,"E0.left"),sQuery(id+"F4.wireOp",EDGE,"E2.top"),subQ0,sQuery(id+"F6.wireOp",EDGE,"E3.top"),sQuery(id+"F6.wireOp",EDGE,"E3.left")])],"isStart":false}),makeQuery(id+"F22.opExtrude","SWEPT_EDGE",EDGE,{"disambiguationData":[OSD([sQuery(id+"F4.wireOp",EDGE,"E2.bottom"),subQ0])]})]});}
            var Q3;
            Q3=makeQuery(id+"F25.boolean.opBoolean","COPY",EDGE,{"derivedFrom":makeQuery(id+"F25.opExtrude","CAP_EDGE",EDGE,{"disambiguationData":[OSD([sQuery(id+"F0.wireOp",EDGE,"E0.bottom"),sQuery(id+"F0.wireOp",EDGE,"E0.left"),sQuery(id+"F4.wireOp",EDGE,"E2.bottom"),sQuery(id+"F4.wireOp",EDGE,"E2.left"),sQuery(id+"F4.wireOp",EDGE,"E2.right")])],"isStart":false})});
            var Q4;
            {var subQ0=sQuery(id+"F6.wireOp",EDGE,"E3.bottom");Q4=makeQuery(id+"F20.boolean.opBoolean","MERGE",EDGE,{"derivedFrom":[makeQuery(id+"F19.boolean.opBoolean","COPY",EDGE,{"derivedFrom":makeQuery(id+"F19.opExtrude","CAP_EDGE",EDGE,{"disambiguationData":[OSD([sQuery(id+"F0.wireOp",EDGE,"E0.bottom"),sQuery(id+"F0.wireOp",EDGE,"E0.left"),subQ0,sQuery(id+"F6.wireOp",EDGE,"E3.right")])],"isStart":false})}),makeQuery(id+"F20.opExtrude","SWEPT_EDGE",EDGE,{"disambiguationData":[OSD([subQ0,sQuery(id+"F6.wireOp",EDGE,"E3.left")])]})]});}
            var Q5;
            Q5=makeQuery(id+"F19.boolean.opBoolean","COPY",EDGE,{"derivedFrom":makeQuery(id+"F19.opExtrude","CAP_EDGE",EDGE,{"disambiguationData":[OSD([sQuery(id+"F0.wireOp",EDGE,"E0.bottom"),sQuery(id+"F0.wireOp",EDGE,"E0.left"),sQuery(id+"F6.wireOp",EDGE,"E4.bottom"),sQuery(id+"F6.wireOp",EDGE,"E4.right")])],"isStart":false})});
            var Q6;
            {var subQ0=sQuery(id+"F0.wireOp",EDGE,"E0.left");var subQ1=sQuery(id+"F0.wireOp",EDGE,"E0.bottom");Q6=makeQuery(id+"F22.boolean.opBoolean","MERGE",FACE,{"derivedFrom":[makeQuery(id+"F20.boolean.opBoolean","MERGE",FACE,{"derivedFrom":[makeQuery(id+"F3.boolean.opBoolean","MERGE",FACE,{"derivedFrom":[makeQuery(id+"F2.boolean.opBoolean","MERGE",FACE,{"derivedFrom":[makeQuery(id+"F1.opExtrude","CAP_FACE",FACE,{"disambiguationData":[OSD([subQ1,sQuery(id+"F0.wireOp",EDGE,"E0.top"),subQ0,sQuery(id+"F0.wireOp",EDGE,"E0.right")])],"isStart":true}),makeQuery(id+"F2.opExtrude","SWEPT_FACE",FACE,{"disambiguationData":[OSD([subQ0]),TDD([makeQuery(id+"F1.opExtrude","CAP_EDGE",EDGE,{"disambiguationData":[OSD([subQ0])],"isStart":true})])]})]}),makeQuery(id+"F3.opExtrude","SWEPT_FACE",FACE,{"disambiguationData":[OSD([subQ1,subQ0]),TDD([makeQuery(id+"F2.boolean.opBoolean","MERGE",EDGE,{"derivedFrom":[makeQuery(id+"F1.opExtrude","CAP_EDGE",EDGE,{"disambiguationData":[OSD([subQ1])],"isStart":true}),makeQuery(id+"F2.opExtrude","SWEPT_EDGE",EDGE,{"disambiguationData":[OSD([subQ1,subQ0]),TDD([makeQuery(id+"F1.opExtrude","CAP_VERTEX",VERTEX,{"disambiguationData":[OSD([subQ1,subQ0])],"isStart":true})])]})]})])]})]}),makeQuery(id+"F20.opExtrude","SWEPT_FACE",FACE,{"disambiguationData":[OSD([subQ1,subQ0])]})]}),makeQuery(id+"F22.opExtrude","SWEPT_FACE",FACE,{"disambiguationData":[OSD([subQ1,subQ0])]})]});}
            chamfer(context, id + "F26", {"entities" : qUnion([Q0, Q1, Q2, Q3, Q4, Q5, Q6]), "width" : 1 * mm, "tangentPropagation" : true});
        }
    });
